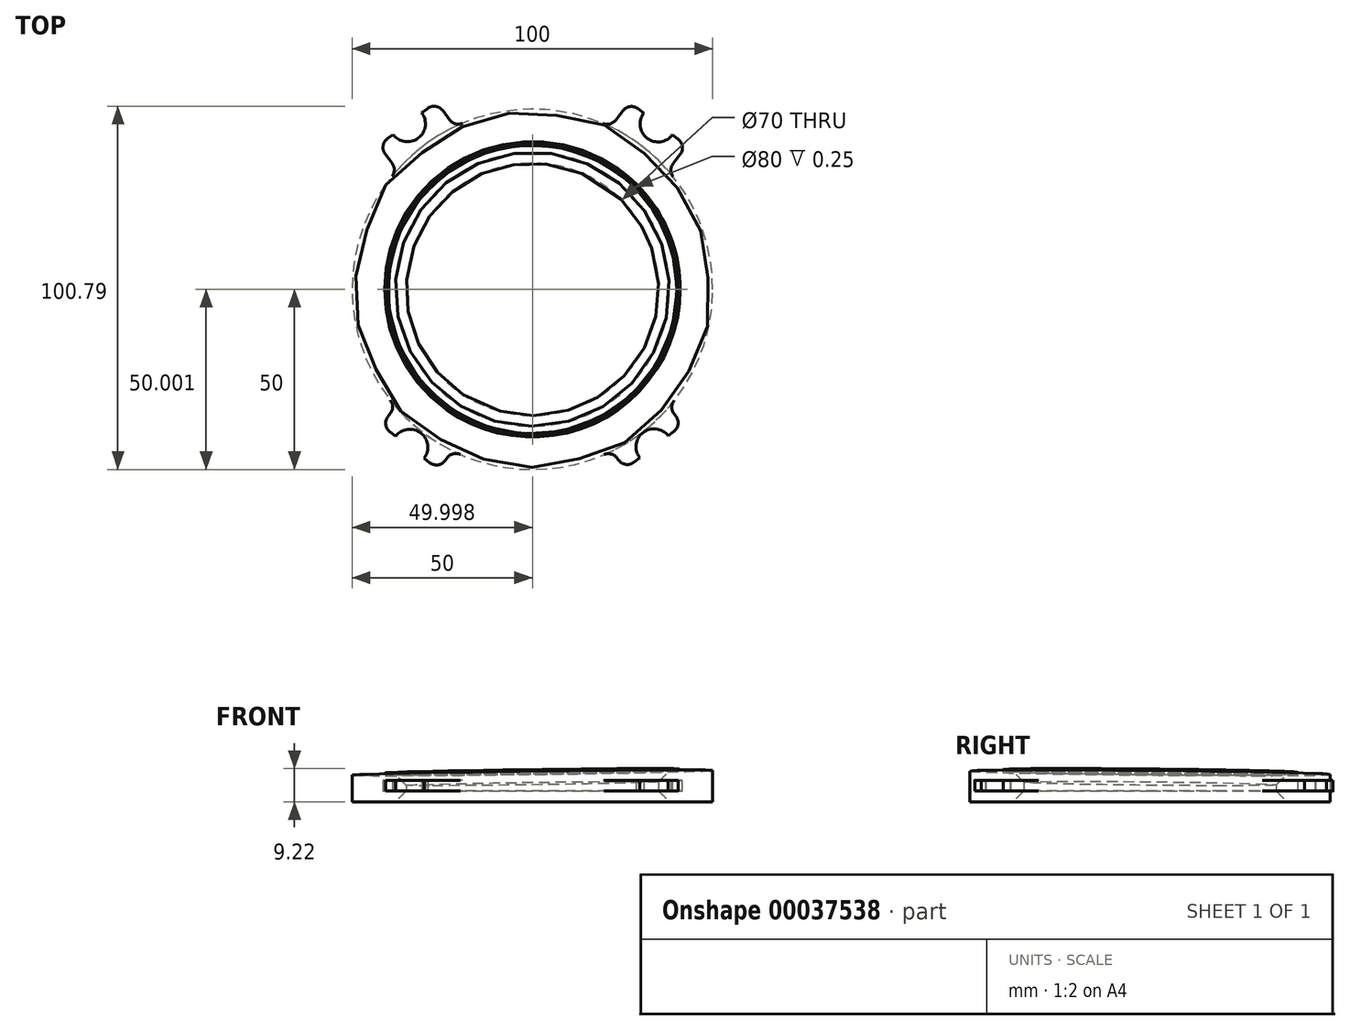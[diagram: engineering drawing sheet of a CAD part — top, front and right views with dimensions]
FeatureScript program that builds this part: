
annotation { "Feature Type Name" : "Feature", "Feature Type Description" : "" }
export const myFeature = defineFeature(function(context is Context, id is Id, definition is map)
    precondition{}
    {
        {
            var Q0;
            Q0=qCreatedBy(makeId("Top.planeOp"),FACE);
            var sketch = newSketch(context, id + "F0", { "sketchPlane" : qUnion([Q0])});
            skLineSegment(sketch, "E0.bottom", {"start": v(-46, 62.5) * mm, "end": v(46, 62.5) * mm});
            skLineSegment(sketch, "E0.top", {"start": v(-46, -57.5) * mm, "end": v(46, -57.5) * mm});
            skLineSegment(sketch, "E0.left", {"start": v(-46, 62.5) * mm, "end": v(-46, -57.5) * mm});
            skLineSegment(sketch, "E0.right", {"start": v(46, 62.5) * mm, "end": v(46, -57.5) * mm});
            skCircle(sketch, "E1", {"center": v(0, 0) * mm, "radius": 37.5 * mm});
            skLineSegment(sketch, "E2", {"start": v(0, 0) * mm, "end": v(0, 62.5) * mm, "construction": true});
            skCircle(sketch, "E3", {"center": v(-34.68, 45.97) * mm, "radius": 4.25 * mm});
            skCircle(sketch, "E4", {"center": v(34.85, 45.9) * mm, "radius": 4.25 * mm});
            skCircle(sketch, "E5", {"center": v(33.71, -43.71) * mm, "radius": 4.25 * mm});
            skCircle(sketch, "E6", {"center": v(-34.03, -43.82) * mm, "radius": 4.25 * mm});
            skSolve(sketch);
        }
        {
            var Q0;
            Q0=sQuery(id+"F0.wireOp",EDGE,"E0.left");
            cPlane(context, id + "F1", {"entities" : qUnion([Q0]), "cplaneType" : CPlaneType.LINE_ANGLE, "offset" : 150 * mm, "angle" : 90 * degree, "width" : 150 * mm, "height" : 150 * mm});
        }
        {
            var Q0;
            Q0=sQuery(id+"F0.wireOp",EDGE,"E0.right");
            cPlane(context, id + "F2", {"entities" : qUnion([Q0]), "cplaneType" : CPlaneType.LINE_ANGLE, "offset" : 150 * mm, "angle" : 90 * degree, "width" : 150 * mm, "height" : 150 * mm});
        }
        {
            var Q0;
            Q0=qCreatedBy(id+"F1.planeOp",FACE);
            var sketch = newSketch(context, id + "F3", { "sketchPlane" : qUnion([Q0])});
            skLineSegment(sketch, "E7", {"start": v(-57.5, 0) * mm, "end": v(-57.5, 5) * mm});
            skLineSegment(sketch, "E8", {"start": v(-57.5, 5) * mm, "end": v(62.53, 4) * mm});
            skLineSegment(sketch, "E9", {"start": v(62.53, 4) * mm, "end": v(62.5, 0) * mm});
            skLineSegment(sketch, "E10", {"start": v(62.5, 0) * mm, "end": v(-57.5, 0) * mm});
            skSolve(sketch);
        }
        {
            var Q0;
            Q0=qCreatedBy(id+"F2.planeOp",FACE);
            var sketch = newSketch(context, id + "F4", { "sketchPlane" : qUnion([Q0])});
            skLineSegment(sketch, "E11", {"start": v(-57.5, 0) * mm, "end": v(-57.5, 6.2) * mm});
            skLineSegment(sketch, "E12", {"start": v(-57.5, 6.2) * mm, "end": v(50.16, 5.2) * mm});
            skLineSegment(sketch, "E13", {"start": v(50.16, 5.2) * mm, "end": v(50.16, 0) * mm});
            skLineSegment(sketch, "E14", {"start": v(50.16, 0) * mm, "end": v(-57.5, 0) * mm});
            skSolve(sketch);
        }
        {
            var Q0;
            Q0=sQuery(id+"F4.wireOp",VERTEX,"E12.start");
            var Q1;
            Q1=sQuery(id+"F4.wireOp",VERTEX,"E13.start");
            var Q2;
            Q2=sQuery(id+"F3.wireOp",VERTEX,"E8.start");
            cPlane(context, id + "F5", {"entities" : qUnion([Q0, Q1, Q2]), "cplaneType" : CPlaneType.THREE_POINT, "offset" : 150 * mm, "width" : 150 * mm, "height" : 150 * mm});
        }
        {
            var Q0;
            Q0=qCreatedBy(makeId("Top.planeOp"),FACE);
            var sketch = newSketch(context, id + "F6", { "sketchPlane" : qUnion([Q0])});
            skCircle(sketch, "E15", {"center": v(0, 0) * mm, "radius": 35 * mm});
            skCircle(sketch, "E16", {"center": v(0, 0) * mm, "radius": 50 * mm});
            skSolve(sketch);
        }
        {
            var Q0;
            Q0=makeQuery(id+"F6.imprint","IMPRINT",FACE,{"disambiguationData":[TD([[makeQuery(id+"F6.imprint","IMPRINT",EDGE,{"derivedFrom":sQuery(id+"F6.wireOp",EDGE,"E15")}),-1.0]])]});
            var Q1;
            Q1=qCreatedBy(id+"F5.planeOp",FACE);
            extrude(context, id + "F7", {"entities" : qUnion([Q0]), "endBound" : BoundingType.UP_TO_SURFACE, "endBoundEntityFace" : qUnion([Q1]), "depth" : 25 * mm, "hasSecondDirection" : true, "secondDirectionOppositeDirection" : true, "secondDirectionDepth" : 3 * mm});
        }
        {
            var Q0;
            Q0=qCreatedBy(makeId("Top.planeOp"),FACE);
            var sketch = newSketch(context, id + "F8", { "sketchPlane" : qUnion([Q0])});
            skLineSegment(sketch, "E17.rect.bottom", {"start": v(13.2, 33.92) * mm, "end": v(29.13, 21.83) * mm});
            skLineSegment(sketch, "E17.rect.top", {"start": v(26.88, 51.95) * mm, "end": v(42.81, 39.85) * mm});
            skLineSegment(sketch, "E17.rect.left", {"start": v(13.2, 33.92) * mm, "end": v(26.88, 51.95) * mm});
            skLineSegment(sketch, "E17.rect.right", {"start": v(29.13, 21.83) * mm, "end": v(42.81, 39.85) * mm});
            skPoint(sketch, "E17.rect.middle", {"position": v(28, 36.89) * mm});
            skLineSegment(sketch, "E18", {"start": v(0, 0) * mm, "end": v(34.85, 45.9) * mm, "construction": true});
            skLineSegment(sketch, "E19", {"start": v(0, 0) * mm, "end": v(-34.68, 45.97) * mm, "construction": true});
            skPoint(sketch, "E20.rect.middle", {"position": v(-27.88, 36.95) * mm});
            skLineSegment(sketch, "E20.rect.right", {"start": v(-13.1, 33.96) * mm, "end": v(-26.7, 52) * mm});
            skLineSegment(sketch, "E20.rect.left", {"start": v(-29.06, 21.92) * mm, "end": v(-42.67, 39.95) * mm});
            skLineSegment(sketch, "E20.rect.top", {"start": v(-42.67, 39.95) * mm, "end": v(-26.7, 52) * mm});
            skLineSegment(sketch, "E20.rect.bottom", {"start": v(-29.06, 21.92) * mm, "end": v(-13.1, 33.96) * mm});
            skLineSegment(sketch, "E21.rect.bottom", {"start": v(29.3, -21.6) * mm, "end": v(13.46, -33.82) * mm});
            skLineSegment(sketch, "E21.rect.top", {"start": v(41.63, -37.6) * mm, "end": v(25.8, -49.82) * mm});
            skLineSegment(sketch, "E21.rect.left", {"start": v(29.3, -21.6) * mm, "end": v(41.63, -37.6) * mm});
            skLineSegment(sketch, "E21.rect.right", {"start": v(13.46, -33.82) * mm, "end": v(25.8, -49.82) * mm});
            skPoint(sketch, "E21.rect.middle", {"position": v(27.54, -35.71) * mm});
            skLineSegment(sketch, "E22", {"start": v(0, 0) * mm, "end": v(33.71, -43.71) * mm, "construction": true});
            skLineSegment(sketch, "E23", {"start": v(0, 0) * mm, "end": v(-34.03, -43.82) * mm, "construction": true});
            skPoint(sketch, "E24.rect.middle", {"position": v(-27.75, -35.73) * mm});
            skLineSegment(sketch, "E24.rect.right", {"start": v(-29.36, -21.51) * mm, "end": v(-41.93, -37.7) * mm});
            skLineSegment(sketch, "E24.rect.left", {"start": v(-13.57, -33.78) * mm, "end": v(-26.13, -49.96) * mm});
            skLineSegment(sketch, "E24.rect.top", {"start": v(-26.13, -49.96) * mm, "end": v(-41.93, -37.7) * mm});
            skLineSegment(sketch, "E24.rect.bottom", {"start": v(-13.57, -33.78) * mm, "end": v(-29.36, -21.51) * mm});
            skSolve(sketch);
        }
        {
            var Q0;
            Q0 = qSketchRegion(id + "F8", true);
            extrude(context, id + "F9", {"entities" : qUnion([Q0]), "operationType" : NewBodyOperationType.ADD, "depth" : 3 * mm});
        }
        {
            var Q0;
            Q0=qCreatedBy(makeId("Top.planeOp"),FACE);
            var sketch = newSketch(context, id + "F10", { "sketchPlane" : qUnion([Q0])});
            skCircle(sketch, "E25", {"center": v(-34.68, 45.97) * mm, "radius": 5 * mm});
            skCircle(sketch, "E26", {"center": v(34.85, 45.9) * mm, "radius": 5 * mm});
            skCircle(sketch, "E27", {"center": v(33.71, -43.71) * mm, "radius": 5 * mm});
            skCircle(sketch, "E28", {"center": v(-34.03, -43.82) * mm, "radius": 5 * mm});
            skSolve(sketch);
        }
        {
            var Q0;
            Q0 = qSketchRegion(id + "F10", true);
            extrude(context, id + "F11", {"entities" : qUnion([Q0]), "operationType" : NewBodyOperationType.REMOVE, "endBound" : BoundingType.THROUGH_ALL, "depth" : 25 * mm, "hasSecondDirection" : true, "secondDirectionBound" : SecondDirectionBoundingType.THROUGH_ALL, "secondDirectionOppositeDirection" : true, "secondDirectionDepth" : 25 * mm});
        }
        {
            var Q0;
            Q0=makeQuery(id+"F9.opExtrude","SWEPT_EDGE",EDGE,{"disambiguationData":[OSD([sQuery(id+"F8.wireOp",EDGE,"E24.rect.left"),sQuery(id+"F8.wireOp",EDGE,"E24.rect.top")])]});
            var Q1;
            Q1=makeQuery(id+"F9.boolean.opBoolean","INTERSECT",EDGE,{"derivedFrom":[makeQuery(id+"F7.opExtrude","SWEPT_FACE",FACE,{"disambiguationData":[OSD([sQuery(id+"F6.wireOp",EDGE,"E16")])]}),makeQuery(id+"F9.opExtrude","SWEPT_FACE",FACE,{"disambiguationData":[OSD([sQuery(id+"F8.wireOp",EDGE,"E24.rect.left")])]})]});
            var Q2;
            Q2=makeQuery(id+"F9.boolean.opBoolean","INTERSECT",EDGE,{"derivedFrom":[makeQuery(id+"F7.opExtrude","SWEPT_FACE",FACE,{"disambiguationData":[OSD([sQuery(id+"F6.wireOp",EDGE,"E16")])]}),makeQuery(id+"F9.opExtrude","SWEPT_FACE",FACE,{"disambiguationData":[OSD([sQuery(id+"F8.wireOp",EDGE,"E24.rect.right")])]})]});
            var Q3;
            Q3=makeQuery(id+"F9.opExtrude","SWEPT_EDGE",EDGE,{"disambiguationData":[OSD([sQuery(id+"F8.wireOp",EDGE,"E24.rect.right"),sQuery(id+"F8.wireOp",EDGE,"E24.rect.top")])]});
            var Q4;
            Q4=makeQuery(id+"F9.opExtrude","SWEPT_EDGE",EDGE,{"disambiguationData":[OSD([sQuery(id+"F8.wireOp",EDGE,"E20.rect.right"),sQuery(id+"F8.wireOp",EDGE,"E20.rect.top")])]});
            var Q5;
            Q5=makeQuery(id+"F9.opExtrude","SWEPT_EDGE",EDGE,{"disambiguationData":[OSD([sQuery(id+"F8.wireOp",EDGE,"E20.rect.left"),sQuery(id+"F8.wireOp",EDGE,"E20.rect.top")])]});
            var Q6;
            Q6=makeQuery(id+"F9.boolean.opBoolean","INTERSECT",EDGE,{"derivedFrom":[makeQuery(id+"F7.opExtrude","SWEPT_FACE",FACE,{"disambiguationData":[OSD([sQuery(id+"F6.wireOp",EDGE,"E16")])]}),makeQuery(id+"F9.opExtrude","SWEPT_FACE",FACE,{"disambiguationData":[OSD([sQuery(id+"F8.wireOp",EDGE,"E20.rect.right")])]})]});
            var Q7;
            Q7=makeQuery(id+"F9.boolean.opBoolean","INTERSECT",EDGE,{"derivedFrom":[makeQuery(id+"F7.opExtrude","SWEPT_FACE",FACE,{"disambiguationData":[OSD([sQuery(id+"F6.wireOp",EDGE,"E16")])]}),makeQuery(id+"F9.opExtrude","SWEPT_FACE",FACE,{"disambiguationData":[OSD([sQuery(id+"F8.wireOp",EDGE,"E20.rect.left")])]})]});
            var Q8;
            Q8=makeQuery(id+"F9.opExtrude","SWEPT_EDGE",EDGE,{"disambiguationData":[OSD([sQuery(id+"F8.wireOp",EDGE,"E17.rect.top"),sQuery(id+"F8.wireOp",EDGE,"E17.rect.left")])]});
            var Q9;
            Q9=makeQuery(id+"F9.boolean.opBoolean","INTERSECT",EDGE,{"derivedFrom":[makeQuery(id+"F7.opExtrude","SWEPT_FACE",FACE,{"disambiguationData":[OSD([sQuery(id+"F6.wireOp",EDGE,"E16")])]}),makeQuery(id+"F9.opExtrude","SWEPT_FACE",FACE,{"disambiguationData":[OSD([sQuery(id+"F8.wireOp",EDGE,"E17.rect.left")])]})]});
            var Q10;
            Q10=makeQuery(id+"F9.opExtrude","SWEPT_EDGE",EDGE,{"disambiguationData":[OSD([sQuery(id+"F8.wireOp",EDGE,"E17.rect.top"),sQuery(id+"F8.wireOp",EDGE,"E17.rect.right")])]});
            var Q11;
            Q11=makeQuery(id+"F9.boolean.opBoolean","INTERSECT",EDGE,{"derivedFrom":[makeQuery(id+"F7.opExtrude","SWEPT_FACE",FACE,{"disambiguationData":[OSD([sQuery(id+"F6.wireOp",EDGE,"E16")])]}),makeQuery(id+"F9.opExtrude","SWEPT_FACE",FACE,{"disambiguationData":[OSD([sQuery(id+"F8.wireOp",EDGE,"E17.rect.right")])]})]});
            var Q12;
            Q12=makeQuery(id+"F9.opExtrude","SWEPT_EDGE",EDGE,{"disambiguationData":[OSD([sQuery(id+"F8.wireOp",EDGE,"E21.rect.top"),sQuery(id+"F8.wireOp",EDGE,"E21.rect.left")])]});
            var Q13;
            Q13=makeQuery(id+"F9.boolean.opBoolean","INTERSECT",EDGE,{"derivedFrom":[makeQuery(id+"F7.opExtrude","SWEPT_FACE",FACE,{"disambiguationData":[OSD([sQuery(id+"F6.wireOp",EDGE,"E16")])]}),makeQuery(id+"F9.opExtrude","SWEPT_FACE",FACE,{"disambiguationData":[OSD([sQuery(id+"F8.wireOp",EDGE,"E21.rect.left")])]})]});
            var Q14;
            Q14=makeQuery(id+"F9.boolean.opBoolean","INTERSECT",EDGE,{"derivedFrom":[makeQuery(id+"F7.opExtrude","SWEPT_FACE",FACE,{"disambiguationData":[OSD([sQuery(id+"F6.wireOp",EDGE,"E16")])]}),makeQuery(id+"F9.opExtrude","SWEPT_FACE",FACE,{"disambiguationData":[OSD([sQuery(id+"F8.wireOp",EDGE,"E21.rect.right")])]})]});
            var Q15;
            Q15=makeQuery(id+"F9.opExtrude","SWEPT_EDGE",EDGE,{"disambiguationData":[OSD([sQuery(id+"F8.wireOp",EDGE,"E21.rect.top"),sQuery(id+"F8.wireOp",EDGE,"E21.rect.right")])]});
            fillet(context, id + "F12", {"entities" : qUnion([Q0, Q1, Q2, Q3, Q4, Q5, Q6, Q7, Q8, Q9, Q10, Q11, Q12, Q13, Q14, Q15]), "radius" : 3 * mm, "tangentPropagation" : true, "allowEdgeOverflow" : false});
        }
        {
            var Q0;
            Q0=makeQuery(id+"F7.opExtrude","CAP_FACE",FACE,{"disambiguationData":[OSD([sQuery(id+"F6.wireOp",EDGE,"E15"),sQuery(id+"F6.wireOp",EDGE,"E16")])],"isStart":true});
            var sketch = newSketch(context, id + "F13", { "sketchPlane" : qUnion([Q0])});
            skCircle(sketch, "E29", {"center": v(0, 0) * mm, "radius": 40 * mm});
            skCircle(sketch, "E30", {"center": v(0, 0) * mm, "radius": 41 * mm});
            skSolve(sketch);
        }
        {
            var Q0;
            Q0=makeQuery(id+"F7.opExtrude","CAP_FACE",FACE,{"disambiguationData":[OSD([sQuery(id+"F6.wireOp",EDGE,"E15"),sQuery(id+"F6.wireOp",EDGE,"E16")])],"isStart":false});
            var sketch = newSketch(context, id + "F14", { "sketchPlane" : qUnion([Q0])});
            skCircle(sketch, "E31", {"center": v(0.07, -0.05) * mm, "radius": 40 * mm});
            skCircle(sketch, "E32", {"center": v(0.07, -0.05) * mm, "radius": 41 * mm});
            skSolve(sketch);
        }
        {
            var Q0;
            Q0 = qSketchRegion(id + "F14", true);
            extrude(context, id + "F15", {"entities" : qUnion([Q0]), "operationType" : NewBodyOperationType.ADD, "depth" : 0.5 * mm});
        }
        {
            var Q0;
            Q0=makeQuery(id+"F15.opExtrude","CAP_FACE",FACE,{"disambiguationData":[OSD([sQuery(id+"F14.wireOp",EDGE,"E31"),sQuery(id+"F14.wireOp",EDGE,"E32")])],"isStart":false});
            chamfer(context, id + "F16", {"entities" : qUnion([Q0]), "width" : 0.25 * mm, "tangentPropagation" : true});
        }
        {
            var Q0;
            Q0=makeQuery(id+"F7.opExtrude","SWEPT_FACE",FACE,{"disambiguationData":[OSD([sQuery(id+"F6.wireOp",EDGE,"E15")])]});
            chamfer(context, id + "F17", {"entities" : qUnion([Q0]), "width" : 3 * mm, "tangentPropagation" : true});
        }
    });
